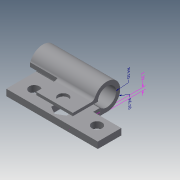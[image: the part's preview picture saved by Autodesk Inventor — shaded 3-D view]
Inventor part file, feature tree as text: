
AUTODESK INVENTOR PART (.ipt)
format: ipt  version: 2019 (Build 230136000, 136)  size: 456,704 bytes
history: native  units: mm
features: extrude x24, sketch x22, other x10, plane x9, projected_geometry x7, direct_edit x5, move_body x4, reference x3, fillet x2, split x2, boolean_combine x1
ambient origin geometry x8: Origin, YZ Plane, XZ Plane, XY Plane, X Axis, Y Axis, Z Axis, Center Point
bodies: Solid1 (feature_tree), Solid2 (feature_tree), Solid3 (feature_tree), Solid4 (feature_tree), Solid5 (feature_tree)
feature tree (89):
  other  "Annotations"
  extrude  "Extrusion1"  Depth=45.0mm
  extrude  "Extrusion4"  Depth=5.0mm
  fillet  "Fillet1"  Radius=11.0mm
  extrude  "Extrusion5"  Depth=23.0mm
  plane  "Work Plane1"
  extrude  "Extrusion6"  Depth=10.0mm
  direct_edit  "Direct Edit1"
  extrude  "Extrusion7"  Depth=12.0mm
  fillet  "Fillet2"  Radius=5.0mm
  plane  "Work Plane5"
  extrude  "Extrusion8"  Depth=5.0mm
  plane  "Work Plane6"
  extrude  "Extrusion9"  Depth=17.8mm
  sketch  "Sketch12"  dims[d34=5.0mm d35=17.8mm]
  extrude  "Extrusion12"  Depth=8.0mm
  extrude  "Extrusion13"  Depth=30.8mm
  extrude  "Extrusion15"  Depth=3.0mm TaperAngle=0.0deg
  plane  "Work Plane7"
  extrude  "Extrusion16"  TaperAngle=0.0deg  [1 undecoded]
  extrude  "Extrusion17"  Depth=18.0mm
  plane  "Work Plane8"
  plane  "Work Plane9"
  split  "Split1"
  split  "Split2"
  boolean_combine  "Combine1"
  direct_edit  "Direct Edit2"
  extrude  "Extrusion18"  Depth=2.0mm
  extrude  "Extrusion20"  Depth=0.5mm TaperAngle=0.0deg
  extrude  "Extrusion21"  Depth=7.25mm TaperAngle=0.0deg
  extrude  "Extrusion22"  Depth=7.25mm TaperAngle=0.0deg
  extrude  "Extrusion23"  Depth=10.0mm TaperAngle=0.0deg
  extrude  "Extrusion24"  Depth=10.0mm
  direct_edit  "Direct Edit3"
  extrude  "Extrusion25"  [1 undecoded]
  sketch  "Sketch24"  dims[d80=10.0mm d81=0.0mm d82=15.0mm]
  plane  "Work Plane10"
  extrude  "Extrusion26"  Depth=3.15mm TaperAngle=0.0deg
  sketch  "Sketch25"  dims[d83=3.0mm d88=-6.0mm]
  plane  "Work Plane11"
  extrude  "Extrusion27"  TaperAngle=0.0deg  [1 undecoded]
  sketch  "Sketch26"  dims[d89=7.5mm d90=3.15mm d91=0.0mm]
  extrude  "Extrusion28"  TaperAngle=0.0deg  [1 undecoded]
  extrude  "Extrusion29"  Depth=0.3mm
  direct_edit  "Direct Edit4"
  sketch  "Sketch28"  dims[d95=0.0mm d96=0.0mm d97=0.0mm d98=-0.3mm d99=0.3mm d100=0.0mm d101=10.0mm d102=0.0mm d105=10.0mm d106=0.0mm d110=1.45mm d111=0.0mm d112=1.45mm d113=0.0mm d114=1.65mm d115=0.0mm d116=0.105mm d117=0.0mm d118=-0.105mm d119=0.105mm d120=0.0mm d121=0.105mm d122=0.0mm d123=0.105mm d124=0.0mm d125=0.0mm d126=0.0mm d127=0.105mm d128=0.0mm d129=-2.0mm d130=10.0mm d131=0.0mm d132=0.0mm d133=0.0mm d134=1.76mm d84=49.911908mm d85=6.5mm d86=52.109261mm d87=4.5mm]
  plane  "Work Plane12"
  extrude  "Extrusion30"  TaperAngle=0.0deg  [1 undecoded]
  direct_edit  "Direct Edit5"
  sketch  "Sketch1"  dims[d0=6.0mm d1=0.0mm d4=45.0mm]
  sketch  "Sketch5"  dims[d5=5.0mm d6=5.0mm d7=11.0mm]
  sketch  "Sketch6"  dims[d8=11.0mm d9=23.0mm]
  sketch  "Sketch7"  dims[d10=10.0mm d20=13.0mm]
  sketch  "Sketch8"  dims[d24=3.0mm d25=0.0mm d26=12.0mm d27=5.0mm]
  sketch  "Sketch10"  dims[d28=3.0mm d29=0.0mm d33=5.0mm]
  projected_geometry  "Projected Loop2"
  sketch  "Sketch13"  dims[d36=8.0mm d37=17.8mm]
  sketch  "Sketch14"  dims[d38=7.1mm d39=30.8mm]
  sketch  "Sketch15"  dims[d40=7.1mm d41=3.0mm d42=0.0mm]
  sketch  "Sketch17"  dims[d46=0.0mm d47=0.0mm d48=-2.5mm d49=0.0mm d50=0.0mm d51=-2.5mm]
  sketch  "Sketch18"  dims[d52=18.0mm d53=11.0mm]
  sketch  "Sketch19"  dims[d54=2.0mm d55=0.0mm d56=2.0mm]
  projected_geometry  "Projected Loop5"
  sketch  "Sketch20"  dims[d57=0.0mm d58=0.5mm d59=0.0mm]
  projected_geometry  "Projected Loop6"
  sketch  "Sketch21"  dims[d60=0.0mm d61=7.25mm d62=0.0mm]
  projected_geometry  "Projected Loop7"
  sketch  "Sketch22"  dims[d68=5.0mm d69=7.25mm d70=0.0mm]
  projected_geometry  "Projected Loop8"
  sketch  "Sketch23"  dims[d72=2.0mm d73=10.0mm d74=0.0mm]
  reference  "Reference1"
  projected_geometry  "Projected Loop9"
  reference  "Reference3"
  reference  "Reference4"
  sketch  "Sketch27"  dims[d92=2.0mm d93=0.0mm d94=0.0mm]
  projected_geometry  "Projected Loop10"
  other  "Composite1"
  move_body  "Move1"
  move_body  "Move2"
  move_body  "Move3"
  other  "Size1"
  other  "Srf1"
  parser-record x1  (decoder bookkeeping rows leaked as tree rows — omitted from the tree; the rows remain in map.json)
  other  "Cerniera versione 3.iam"
  other  "Cerniera 5.5:1"
  other  "Size2"
  move_body  "Move4"
  other  "Radial Dimension 1"
  other  "Radial Dimension 2"
note: 5 required parameter values undecoded (feature->parameter linkage not recoverable at this tier; creation-order binding heuristic only, values carry confidence <= 0.55)
note: 1 file-system path scrubbed to <path> (originals preserved in map.json)
